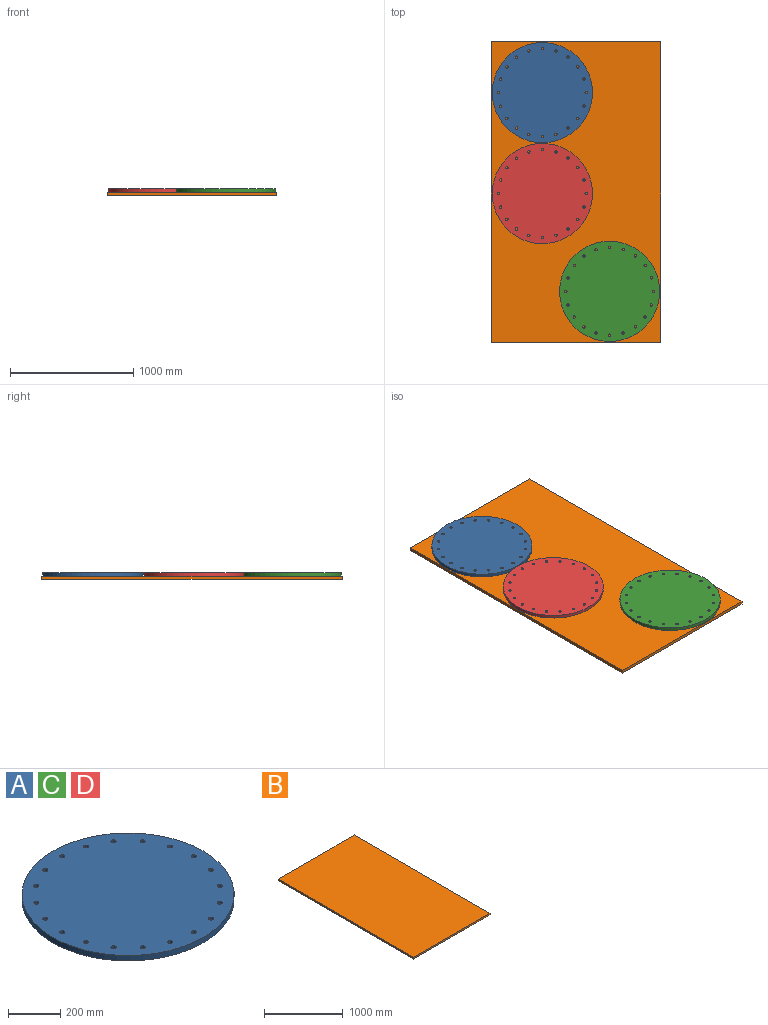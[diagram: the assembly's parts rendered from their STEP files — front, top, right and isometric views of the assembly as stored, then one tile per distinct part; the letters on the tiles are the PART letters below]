
ASSEMBLY  parts=4 mates=2
PART A: 23 faces, bbox 812.8x812.8x25.4 mm
  f0: cylinder r=406.4mm len=812.8mm, axis (0,0,-1), area 64858.6mm2, adj f1,f2
  f1: plane 812.8x812.8mm, normal (0,0,1), area 512928.4mm2, adj f0,f3,f4,f5,f6,f7,f8,f9
  f2: plane 812.8x812.8mm, normal (0,0,-1), area 512928.4mm2, adj f0,f3,f4,f5,f6,f7,f8,f9
  f3: cylinder r=9.72mm len=25.4mm, axis (0,0,1), area 1551.7mm2, adj f1,f2
  f4: cylinder r=9.72mm len=25.4mm, axis (0,0,1), area 1551.7mm2, adj f1,f2
  f5: cylinder r=9.72mm len=25.4mm, axis (0,0,1), area 1551.7mm2, adj f1,f2
  f6: cylinder r=9.72mm len=25.4mm, axis (0,0,1), area 1551.7mm2, adj f1,f2
  f7: cylinder r=9.72mm len=25.4mm, axis (0,0,1), area 1551.7mm2, adj f1,f2
  f8: cylinder r=9.72mm len=25.4mm, axis (0,0,1), area 1551.7mm2, adj f1,f2
  f9: cylinder r=9.72mm len=25.4mm, axis (0,0,1), area 1551.7mm2, adj f1,f2
  f10: cylinder r=9.72mm len=25.4mm, axis (0,0,1), area 1551.7mm2, adj f1,f2
  f11: cylinder r=9.72mm len=25.4mm, axis (0,0,1), area 1551.7mm2, adj f1,f2
  f12: cylinder r=9.72mm len=25.4mm, axis (0,0,1), area 1551.7mm2, adj f1,f2
  f13: cylinder r=9.72mm len=25.4mm, axis (0,0,1), area 1551.7mm2, adj f1,f2
  f14: cylinder r=9.72mm len=25.4mm, axis (0,0,1), area 1551.7mm2, adj f1,f2
  f15: cylinder r=9.72mm len=25.4mm, axis (0,0,1), area 1551.7mm2, adj f1,f2
  f16: cylinder r=9.72mm len=25.4mm, axis (0,0,1), area 1551.7mm2, adj f1,f2
  f17: cylinder r=9.72mm len=25.4mm, axis (0,0,1), area 1551.7mm2, adj f1,f2
  f18: cylinder r=9.72mm len=25.4mm, axis (0,0,1), area 1551.7mm2, adj f1,f2
  f19: cylinder r=9.72mm len=25.4mm, axis (0,0,1), area 1551.7mm2, adj f1,f2
  f20: cylinder r=9.72mm len=25.4mm, axis (0,0,1), area 1551.7mm2, adj f1,f2
  f21: cylinder r=9.72mm len=25.4mm, axis (0,0,1), area 1551.7mm2, adj f1,f2
  f22: cylinder r=9.72mm len=25.4mm, axis (0,0,1), area 1551.7mm2, adj f1,f2
PART B: 6 faces, bbox 1371.6x2438.4x25.4 mm
  f0: plane 2438.4x25.4mm, normal (-1,0,0), area 61935.4mm2, adj f1,f3,f4,f5
  f1: plane 1371.6x25.4mm, normal (0,-1,0), area 34838.6mm2, adj f0,f2,f4,f5
  f2: plane 2438.4x25.4mm, normal (1,0,0), area 61935.4mm2, adj f1,f3,f4,f5
  f3: plane 1371.6x25.4mm, normal (0,1,0), area 34838.6mm2, adj f0,f2,f4,f5
  f4: plane 2438.4x1371.6mm, normal (0,0,1), area 3344509.4mm2, adj f0,f1,f2,f3
  f5: plane 2438.4x1371.6mm, normal (0,0,-1), area 3344509.4mm2, adj f0,f1,f2,f3
PART C: same geometry as A
PART D: same geometry as A
PLACE A rot(axis=(1,0,0),180deg) t=(940.31,1604.23,345.63)mm
PLACE B t=(527.56,-421.42,294.83)mm
PLACE C rot(axis=(1,0,0),180deg) t=(1486.41,-8.67,345.63)mm
PLACE D rot(axis=(1,0,0),180deg) t=(940.31,785.08,345.63)mm
MATE fastened C.f0 <-> B.f4  axis (0,0,-1) through (1486.41,-8.67,320.23)mm
MATE fastened A.f0 <-> B.f4  axis (0,0,-1) through (940.31,1604.23,320.23)mm
